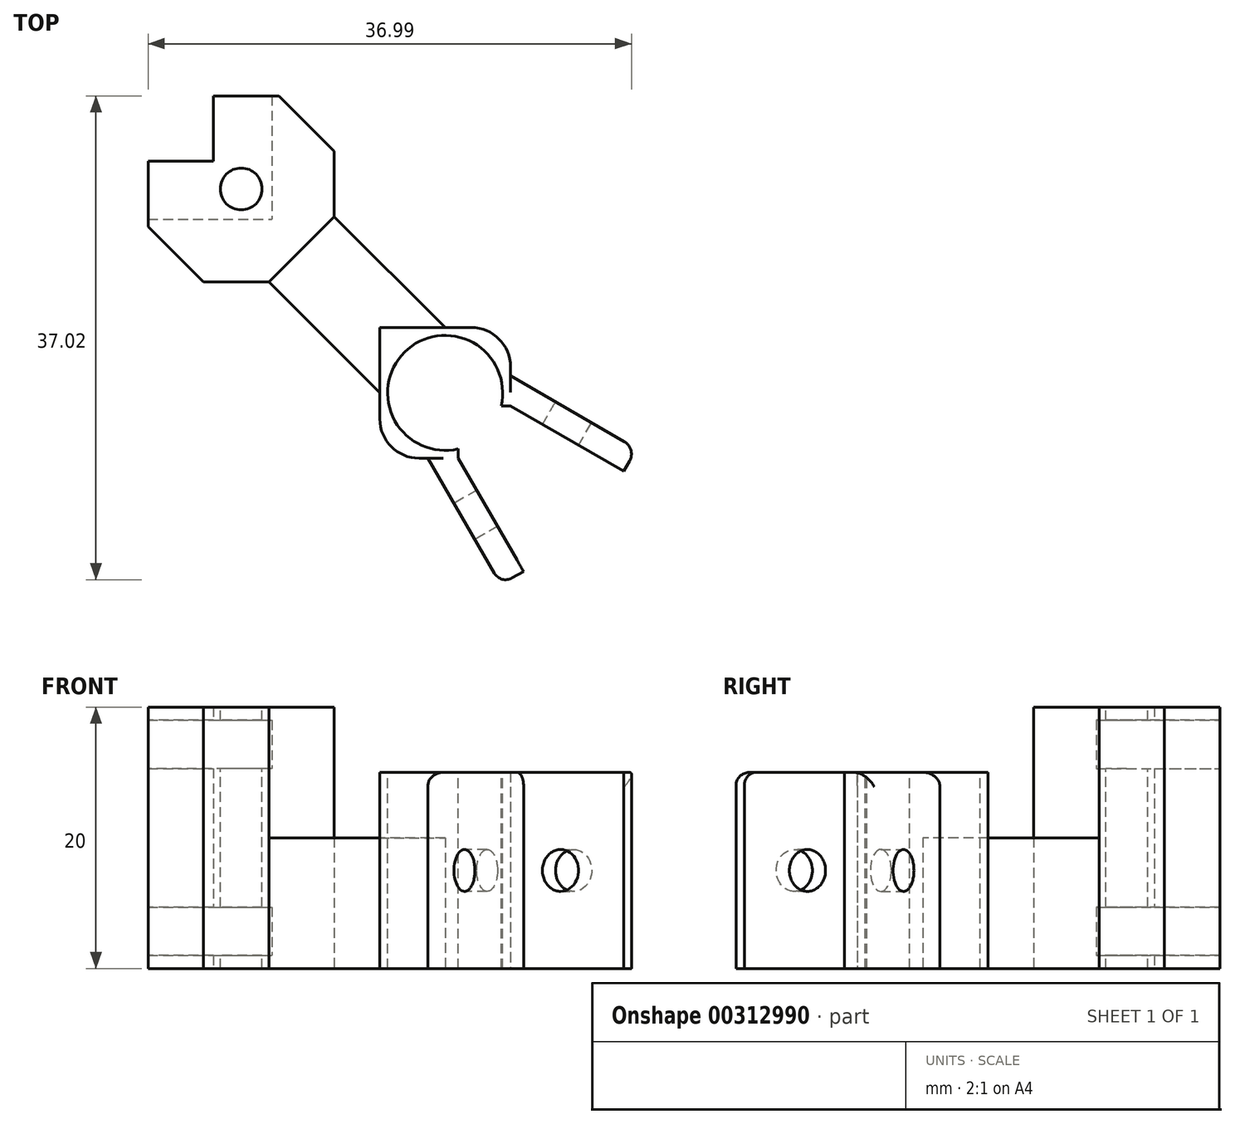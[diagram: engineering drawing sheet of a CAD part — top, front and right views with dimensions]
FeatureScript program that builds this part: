
annotation { "Feature Type Name" : "Feature", "Feature Type Description" : "" }
export const myFeature = defineFeature(function(context is Context, id is Id, definition is map)
    precondition{}
    {
        {
            var Q0;
            Q0=qCreatedBy(makeId("Top.planeOp"),FACE);
            var sketch = newSketch(context, id + "F0", { "sketchPlane" : qUnion([Q0])});
            skLineSegment(sketch, "E0", {"start": v(0, 0) * mm, "end": v(-5, 0) * mm});
            skLineSegment(sketch, "E1", {"start": v(-5, 0) * mm, "end": v(-5, 5) * mm});
            skLineSegment(sketch, "E2", {"start": v(-5, 5) * mm, "end": v(0, 5) * mm});
            skLineSegment(sketch, "E3", {"start": v(0, 5) * mm, "end": v(0, 10) * mm});
            skLineSegment(sketch, "E4", {"start": v(0, 10) * mm, "end": v(5, 10) * mm});
            skLineSegment(sketch, "E5", {"start": v(5, 10) * mm, "end": v(5, 5) * mm});
            skLineSegment(sketch, "E6", {"start": v(-5, 0) * mm, "end": v(-0.76, -4.24) * mm});
            skLineSegment(sketch, "E7", {"start": v(5, 10) * mm, "end": v(9.24, 5.76) * mm});
            skLineSegment(sketch, "E8", {"start": v(9.24, 5.76) * mm, "end": v(9.24, 0.76) * mm});
            skLineSegment(sketch, "E9", {"start": v(-0.76, -4.24) * mm, "end": v(4.24, -4.24) * mm});
            skLineSegment(sketch, "E10", {"start": v(9.24, 0.76) * mm, "end": v(17.73, -7.73) * mm});
            skLineSegment(sketch, "E11", {"start": v(4.24, -4.24) * mm, "end": v(12.73, -12.73) * mm});
            skLineSegment(sketch, "E12", {"start": v(12.73, -12.73) * mm, "end": v(12.73, -17.73) * mm});
            skLineSegment(sketch, "E13", {"start": v(12.73, -17.73) * mm, "end": v(22.73, -17.73) * mm});
            skLineSegment(sketch, "E14", {"start": v(22.73, -17.73) * mm, "end": v(22.73, -7.73) * mm});
            skLineSegment(sketch, "E15", {"start": v(22.73, -7.73) * mm, "end": v(17.73, -7.73) * mm});
            skLineSegment(sketch, "E16", {"start": v(4.24, -4.24) * mm, "end": v(9.24, 0.76) * mm});
            skPoint(sketch, "E17", {"position": v(22.73, -13.73) * mm});
            skPoint(sketch, "E18", {"position": v(18.73, -17.73) * mm});
            skLineSegment(sketch, "E19", {"start": v(22.73, -13.73) * mm, "end": v(31.39, -18.73) * mm});
            skLineSegment(sketch, "E20", {"start": v(18.73, -17.73) * mm, "end": v(23.73, -26.39) * mm});
            skLineSegment(sketch, "E21", {"start": v(31.39, -18.73) * mm, "end": v(32.39, -17) * mm});
            skLineSegment(sketch, "E22", {"start": v(32.39, -17) * mm, "end": v(22.73, -11.42) * mm});
            skLineSegment(sketch, "E23", {"start": v(23.73, -26.39) * mm, "end": v(22, -27.39) * mm});
            skLineSegment(sketch, "E24", {"start": v(22, -27.39) * mm, "end": v(16.42, -17.73) * mm});
            skSolve(sketch);
        }
        {
            var Q0;
            Q0=makeQuery(id+"F0.imprint","IMPRINT",FACE,{"disambiguationData":[TD([[makeQuery(id+"F0.imprint","IMPRINT",EDGE,{"derivedFrom":sQuery(id+"F0.wireOp",EDGE,"E1")}),-1.0]])]});
            extrude(context, id + "F1", {"entities" : qUnion([Q0]), "depth" : 20 * mm});
        }
        {
            var Q0;
            Q0=makeQuery(id+"F0.imprint","IMPRINT",FACE,{"disambiguationData":[TD([[makeQuery(id+"F0.imprint","IMPRINT",EDGE,{"derivedFrom":sQuery(id+"F0.wireOp",EDGE,"E10")}),-1.0]])]});
            extrude(context, id + "F2", {"entities" : qUnion([Q0]), "operationType" : NewBodyOperationType.ADD, "depth" : 10 * mm});
        }
        {
            var Q0;
            Q0=makeQuery(id+"F1.opExtrude","SWEPT_FACE",FACE,{"disambiguationData":[OSD([sQuery(id+"F0.wireOp",EDGE,"E4")])]});
            var sketch = newSketch(context, id + "F3", { "sketchPlane" : qUnion([Q0])});
            skPoint(sketch, "E25", {"position": v(0, 19) * mm});
            skPoint(sketch, "E26", {"position": v(0, 15.6) * mm});
            skPoint(sketch, "E27", {"position": v(0, 1) * mm});
            skPoint(sketch, "E28", {"position": v(0, 4.4) * mm});
            skLineSegment(sketch, "E29", {"start": v(0, 19) * mm, "end": v(-5, 19) * mm});
            skLineSegment(sketch, "E30", {"start": v(-5, 19) * mm, "end": v(-5, 15.6) * mm});
            skLineSegment(sketch, "E31", {"start": v(-5, 15.6) * mm, "end": v(0, 15.6) * mm});
            skSolve(sketch);
        }
        {
            var Q0;
            Q0=qSketchRegion(id+"F3",true);
            var Q1;
            {var subQ0=sQuery(id+"F3.wireOp",EDGE,"E29");Q1=makeQuery(id+"F3.imprint","IMPRINT",FACE,{"disambiguationData":[TD([[makeQuery(id+"F3.imprint","IMPRINT",EDGE,{"derivedFrom":subQ0}),1.0]])]});}
            extrude(context, id + "F4", {"entities" : qUnion([Q0, Q1]), "operationType" : NewBodyOperationType.REMOVE, "oppositeDirection" : true, "depth" : 25 * mm});
        }
        {
            var Q0;
            Q0=makeQuery(id+"F1.opExtrude","SWEPT_FACE",FACE,{"disambiguationData":[OSD([sQuery(id+"F0.wireOp",EDGE,"E2")])]});
            var sketch = newSketch(context, id + "F5", { "sketchPlane" : qUnion([Q0])});
            skLineSegment(sketch, "E32", {"start": v(0, 19) * mm, "end": v(5, 19) * mm});
            skLineSegment(sketch, "E33", {"start": v(5, 19) * mm, "end": v(5, 15.6) * mm});
            skLineSegment(sketch, "E34", {"start": v(5, 15.6) * mm, "end": v(0, 15.6) * mm});
            skLineSegment(sketch, "E35", {"start": v(0, 15.6) * mm, "end": v(0, 19) * mm});
            skSolve(sketch);
        }
        {
            var Q0;
            Q0=makeQuery(id+"F5.imprint","IMPRINT",FACE,{"disambiguationData":[TD([[makeQuery(id+"F5.imprint","IMPRINT",EDGE,{"derivedFrom":sQuery(id+"F5.wireOp",EDGE,"E32")}),-1.0]])]});
            extrude(context, id + "F6", {"entities" : qUnion([Q0]), "operationType" : NewBodyOperationType.REMOVE, "oppositeDirection" : true, "depth" : 25 * mm});
        }
        {
            var Q0;
            Q0=makeQuery(id+"F1.opExtrude","SWEPT_FACE",FACE,{"disambiguationData":[OSD([sQuery(id+"F0.wireOp",EDGE,"E7")])]});
            var sketch = newSketch(context, id + "F7", { "sketchPlane" : qUnion([Q0])});
            skLineSegment(sketch, "E36", {"start": v(3.54, 15.6) * mm, "end": v(-2.46, 15.6) * mm});
            skLineSegment(sketch, "E37", {"start": v(-2.46, 15.6) * mm, "end": v(-2.46, 19) * mm});
            skLineSegment(sketch, "E38", {"start": v(-2.46, 19) * mm, "end": v(3.54, 19) * mm});
            skLineSegment(sketch, "E39", {"start": v(3.54, 19) * mm, "end": v(3.54, 15.6) * mm});
            skSolve(sketch);
        }
        {
            var Q0;
            Q0=qSketchRegion(id+"F7",true);
            extrude(context, id + "F8", {"entities" : qUnion([Q0]), "operationType" : NewBodyOperationType.REMOVE, "oppositeDirection" : true, "depth" : 25 * mm});
        }
        {
            var Q0;
            {var subQ3=sQuery(id+"F0.wireOp",EDGE,"E4");Q0=makeQuery(id+"F4.boolean.opBoolean","SPLIT",FACE,{"disambiguationData":[TD([makeQuery(id+"F4.opExtrude","SWEPT_FACE",FACE,{"disambiguationData":[OSD([sQuery(id+"F3.wireOp",EDGE,"E31")])]})])],"derivedFrom":makeQuery(id+"F1.opExtrude","SWEPT_FACE",FACE,{"disambiguationData":[OSD([subQ3])]})});}
            var sketch = newSketch(context, id + "F9", { "sketchPlane" : qUnion([Q0])});
            skPoint(sketch, "E40", {"position": v(0, 1) * mm});
            skPoint(sketch, "E41", {"position": v(0, 4.4) * mm});
            skLineSegment(sketch, "E42.bottom", {"start": v(0, 4.4) * mm, "end": v(-5, 4.4) * mm});
            skLineSegment(sketch, "E42.top", {"start": v(0, 1) * mm, "end": v(-5, 1) * mm});
            skLineSegment(sketch, "E42.left", {"start": v(0, 4.4) * mm, "end": v(0, 1) * mm});
            skLineSegment(sketch, "E42.right", {"start": v(-5, 4.4) * mm, "end": v(-5, 1) * mm});
            skSolve(sketch);
        }
        {
            var Q0;
            Q0=qSketchRegion(id+"F9",true);
            extrude(context, id + "F10", {"entities" : qUnion([Q0]), "operationType" : NewBodyOperationType.REMOVE, "oppositeDirection" : true, "depth" : 25 * mm});
        }
        {
            var Q0;
            {var subQ3=sQuery(id+"F0.wireOp",EDGE,"E7");Q0=makeQuery(id+"F8.boolean.opBoolean","SPLIT",FACE,{"disambiguationData":[TD([makeQuery(id+"F4.boolean.opBoolean","COPY",FACE,{"derivedFrom":makeQuery(id+"F4.opExtrude","SWEPT_FACE",FACE,{"disambiguationData":[OSD([sQuery(id+"F3.wireOp",EDGE,"E31")])]})})])],"derivedFrom":makeQuery(id+"F1.opExtrude","SWEPT_FACE",FACE,{"disambiguationData":[OSD([subQ3])]})});}
            var sketch = newSketch(context, id + "F11", { "sketchPlane" : qUnion([Q0])});
            skLineSegment(sketch, "E43.bottom", {"start": v(3.54, 1) * mm, "end": v(-2.46, 1) * mm});
            skLineSegment(sketch, "E43.top", {"start": v(3.54, 4.4) * mm, "end": v(-2.46, 4.4) * mm});
            skLineSegment(sketch, "E43.left", {"start": v(3.54, 1) * mm, "end": v(3.54, 4.4) * mm});
            skLineSegment(sketch, "E43.right", {"start": v(-2.46, 1) * mm, "end": v(-2.46, 4.4) * mm});
            skSolve(sketch);
        }
        {
            var Q0;
            Q0=qSketchRegion(id+"F11",true);
            extrude(context, id + "F12", {"entities" : qUnion([Q0]), "operationType" : NewBodyOperationType.REMOVE, "oppositeDirection" : true, "depth" : 25 * mm});
        }
        {
            var Q0;
            {var subQ2=sQuery(id+"F0.wireOp",EDGE,"E2");Q0=makeQuery(id+"F6.boolean.opBoolean","SPLIT",FACE,{"disambiguationData":[TD([makeQuery(id+"F4.boolean.opBoolean","COPY",FACE,{"derivedFrom":makeQuery(id+"F4.opExtrude","SWEPT_FACE",FACE,{"disambiguationData":[OSD([sQuery(id+"F3.wireOp",EDGE,"E31")])]})})])],"derivedFrom":makeQuery(id+"F1.opExtrude","SWEPT_FACE",FACE,{"disambiguationData":[OSD([subQ2])]})});}
            var sketch = newSketch(context, id + "F13", { "sketchPlane" : qUnion([Q0])});
            skLineSegment(sketch, "E44.bottom", {"start": v(0, 4.4) * mm, "end": v(5, 4.4) * mm});
            skLineSegment(sketch, "E44.top", {"start": v(0, 1) * mm, "end": v(5, 1) * mm});
            skLineSegment(sketch, "E44.left", {"start": v(0, 4.4) * mm, "end": v(0, 1) * mm});
            skLineSegment(sketch, "E44.right", {"start": v(5, 4.4) * mm, "end": v(5, 1) * mm});
            skSolve(sketch);
        }
        {
            var Q0;
            Q0=qSketchRegion(id+"F13",true);
            extrude(context, id + "F14", {"entities" : qUnion([Q0]), "operationType" : NewBodyOperationType.REMOVE, "oppositeDirection" : true, "depth" : 25 * mm});
        }
        {
            var Q0;
            Q0=makeQuery(id+"F1.opExtrude","CAP_FACE",FACE,{"disambiguationData":[OSD([sQuery(id+"F0.wireOp",EDGE,"E1"),sQuery(id+"F0.wireOp",EDGE,"E2"),sQuery(id+"F0.wireOp",EDGE,"E3"),sQuery(id+"F0.wireOp",EDGE,"E4"),sQuery(id+"F0.wireOp",EDGE,"E6"),sQuery(id+"F0.wireOp",EDGE,"E7"),sQuery(id+"F0.wireOp",EDGE,"E8"),sQuery(id+"F0.wireOp",EDGE,"E9"),sQuery(id+"F0.wireOp",EDGE,"E16")])],"isStart":false});
            var sketch = newSketch(context, id + "F15", { "sketchPlane" : qUnion([Q0])});
            skLineSegment(sketch, "E45", {"start": v(0, 5) * mm, "end": v(0, 3.17) * mm});
            skLineSegment(sketch, "E46", {"start": v(0, 5) * mm, "end": v(2.05, 5) * mm});
            skLineSegment(sketch, "E47", {"start": v(0, 5) * mm, "end": v(2.12, 2.88) * mm});
            skSolve(sketch);
        }
        {
            var Q0;
            Q0=sQuery(id+"F15.wireOp",VERTEX,"E47.end");
            var Q1;
            Q1=makeQuery(id+"F1.opExtrude","SWEPT_BODY",BODY,{"disambiguationData":[OSD([sQuery(id+"F0.wireOp",EDGE,"E1"),sQuery(id+"F0.wireOp",EDGE,"E2"),sQuery(id+"F0.wireOp",EDGE,"E3"),sQuery(id+"F0.wireOp",EDGE,"E4"),sQuery(id+"F0.wireOp",EDGE,"E6"),sQuery(id+"F0.wireOp",EDGE,"E7"),sQuery(id+"F0.wireOp",EDGE,"E8"),sQuery(id+"F0.wireOp",EDGE,"E9"),sQuery(id+"F0.wireOp",EDGE,"E16")])]});
            hole(context, id + "F16", {"style" : HoleStyle.SIMPLE, "endStyle" : HoleEndStyle.THROUGH, "holeDiameter" : 3.2 * mm, "tappedDepth" : 12 * mm, "tapClearance" : 3, "locations" : qUnion([Q0]), "scope" : qUnion([Q1])});
        }
        {
            var Q0;
            Q0=makeQuery(id+"F2.opExtrude","CAP_FACE",FACE,{"disambiguationData":[OSD([sQuery(id+"F0.wireOp",EDGE,"E10"),sQuery(id+"F0.wireOp",EDGE,"E11"),sQuery(id+"F0.wireOp",EDGE,"E12"),sQuery(id+"F0.wireOp",EDGE,"E13"),sQuery(id+"F0.wireOp",EDGE,"E14"),sQuery(id+"F0.wireOp",EDGE,"E15"),sQuery(id+"F0.wireOp",EDGE,"E16")])],"isStart":false});
            var sketch = newSketch(context, id + "F17", { "sketchPlane" : qUnion([Q0])});
            skLineSegment(sketch, "E48", {"start": v(22.73, -7.73) * mm, "end": v(12.73, -17.73) * mm});
            skLineSegment(sketch, "E49", {"start": v(22.73, -17.73) * mm, "end": v(13.62, -8.62) * mm});
            skPoint(sketch, "E50", {"position": v(17.73, -12.73) * mm});
            skSolve(sketch);
        }
        {
            var Q0;
            Q0=sQuery(id+"F17.wireOp",VERTEX,"E50");
            var Q1;
            Q1=makeQuery(id+"F1.opExtrude","SWEPT_BODY",BODY,{"disambiguationData":[OSD([sQuery(id+"F0.wireOp",EDGE,"E1"),sQuery(id+"F0.wireOp",EDGE,"E2"),sQuery(id+"F0.wireOp",EDGE,"E3"),sQuery(id+"F0.wireOp",EDGE,"E4"),sQuery(id+"F0.wireOp",EDGE,"E6"),sQuery(id+"F0.wireOp",EDGE,"E7"),sQuery(id+"F0.wireOp",EDGE,"E8"),sQuery(id+"F0.wireOp",EDGE,"E9"),sQuery(id+"F0.wireOp",EDGE,"E16")])]});
            hole(context, id + "F18", {"style" : HoleStyle.SIMPLE, "endStyle" : HoleEndStyle.THROUGH, "holeDiameter" : 8.8 * mm, "tappedDepth" : 12 * mm, "tapClearance" : 3, "locations" : qUnion([Q0]), "scope" : qUnion([Q1])});
        }
        {
            var Q0;
            Q0=makeQuery(id+"F2.opExtrude","CAP_FACE",FACE,{"disambiguationData":[OSD([sQuery(id+"F0.wireOp",EDGE,"E10"),sQuery(id+"F0.wireOp",EDGE,"E11"),sQuery(id+"F0.wireOp",EDGE,"E12"),sQuery(id+"F0.wireOp",EDGE,"E13"),sQuery(id+"F0.wireOp",EDGE,"E14"),sQuery(id+"F0.wireOp",EDGE,"E15"),sQuery(id+"F0.wireOp",EDGE,"E16")])],"isStart":false});
            var sketch = newSketch(context, id + "F19", { "sketchPlane" : qUnion([Q0])});
            skLineSegment(sketch, "E51.bottom", {"start": v(22.73, -7.73) * mm, "end": v(12.73, -7.73) * mm});
            skLineSegment(sketch, "E51.top", {"start": v(22.73, -17.73) * mm, "end": v(12.73, -17.73) * mm});
            skLineSegment(sketch, "E51.left", {"start": v(22.73, -7.73) * mm, "end": v(22.73, -17.73) * mm});
            skLineSegment(sketch, "E51.right", {"start": v(12.73, -7.73) * mm, "end": v(12.73, -17.73) * mm});
            skSolve(sketch);
        }
        {
            var Q0;
            {var subQ1=sQuery(id+"F19.wireOp",EDGE,"E51.top");Q0=makeQuery(id+"F19.imprint","IMPRINT",FACE,{"disambiguationData":[TD([[makeQuery(id+"F19.imprint","IMPRINT",EDGE,{"derivedFrom":subQ1}),1.0]])]});}
            extrude(context, id + "F20", {"entities" : qUnion([Q0]), "operationType" : NewBodyOperationType.ADD, "depth" : 5 * mm});
        }
        {
            var Q0;
            Q0=makeQuery(id+"F8.boolean.opBoolean","MERGE",FACE,{"derivedFrom":[makeQuery(id+"F6.boolean.opBoolean","MERGE",FACE,{"derivedFrom":[makeQuery(id+"F4.boolean.opBoolean","COPY",FACE,{"derivedFrom":makeQuery(id+"F4.opExtrude","SWEPT_FACE",FACE,{"disambiguationData":[OSD([sQuery(id+"F3.wireOp",EDGE,"E31")])]})}),makeQuery(id+"F6.opExtrude","SWEPT_FACE",FACE,{"disambiguationData":[OSD([sQuery(id+"F5.wireOp",EDGE,"E34")])]})]}),makeQuery(id+"F8.opExtrude","SWEPT_FACE",FACE,{"disambiguationData":[OSD([sQuery(id+"F7.wireOp",EDGE,"E36")])]})]});
            extrude(context, id + "F21", {"entities" : qUnion([Q0]), "operationType" : NewBodyOperationType.REMOVE, "oppositeDirection" : true, "depth" : 0.3 * mm});
        }
        {
            var Q0;
            Q0=makeQuery(id+"F14.boolean.opBoolean","MERGE",FACE,{"derivedFrom":[makeQuery(id+"F12.boolean.opBoolean","MERGE",FACE,{"derivedFrom":[makeQuery(id+"F10.boolean.opBoolean","COPY",FACE,{"derivedFrom":makeQuery(id+"F10.opExtrude","SWEPT_FACE",FACE,{"disambiguationData":[OSD([sQuery(id+"F9.wireOp",EDGE,"E42.bottom")])]})}),makeQuery(id+"F12.opExtrude","SWEPT_FACE",FACE,{"disambiguationData":[OSD([sQuery(id+"F11.wireOp",EDGE,"E43.top")])]})]}),makeQuery(id+"F14.opExtrude","SWEPT_FACE",FACE,{"disambiguationData":[OSD([sQuery(id+"F13.wireOp",EDGE,"E44.bottom")])]})]});
            extrude(context, id + "F22", {"entities" : qUnion([Q0]), "operationType" : NewBodyOperationType.REMOVE, "oppositeDirection" : true, "depth" : 0.3 * mm});
        }
        {
            var Q0;
            Q0=makeQuery(id+"F20.boolean.opBoolean","MERGE",FACE,{"derivedFrom":[makeQuery(id+"F2.opExtrude","SWEPT_FACE",FACE,{"disambiguationData":[OSD([sQuery(id+"F0.wireOp",EDGE,"E13")])]}),makeQuery(id+"F20.opExtrude","SWEPT_FACE",FACE,{"disambiguationData":[OSD([sQuery(id+"F19.wireOp",EDGE,"E51.top")])]})]});
            var sketch = newSketch(context, id + "F23", { "sketchPlane" : qUnion([Q0])});
            skLineSegment(sketch, "E52", {"start": v(12.79, 15) * mm, "end": v(22.73, 15) * mm});
            skPoint(sketch, "E53", {"position": v(18.73, 15) * mm});
            skLineSegment(sketch, "E54", {"start": v(18.73, 15) * mm, "end": v(18.73, 0) * mm});
            skLineSegment(sketch, "E55", {"start": v(18.73, 0) * mm, "end": v(22.73, 0) * mm});
            skLineSegment(sketch, "E56", {"start": v(22.73, 0) * mm, "end": v(22.73, 15) * mm});
            skSolve(sketch);
        }
        {
            var Q0;
            Q0=makeQuery(id+"F20.boolean.opBoolean","MERGE",FACE,{"derivedFrom":[makeQuery(id+"F2.opExtrude","SWEPT_FACE",FACE,{"disambiguationData":[OSD([sQuery(id+"F0.wireOp",EDGE,"E14")])]}),makeQuery(id+"F20.opExtrude","SWEPT_FACE",FACE,{"disambiguationData":[OSD([sQuery(id+"F19.wireOp",EDGE,"E51.left")])]})]});
            var sketch = newSketch(context, id + "F24", { "sketchPlane" : qUnion([Q0])});
            skLineSegment(sketch, "E57", {"start": v(-17.73, 15) * mm, "end": v(-7.73, 15) * mm});
            skPoint(sketch, "E58", {"position": v(-13.73, 15) * mm});
            skLineSegment(sketch, "E59", {"start": v(-13.73, 15) * mm, "end": v(-13.73, 0) * mm});
            skLineSegment(sketch, "E60", {"start": v(-13.73, 0) * mm, "end": v(-17.73, 0) * mm});
            skLineSegment(sketch, "E61", {"start": v(-17.73, 0) * mm, "end": v(-17.73, 15) * mm});
            skSolve(sketch);
        }
        {
            var Q0;
            Q0=qSketchRegion(id+"F24",true);
            extrude(context, id + "F25", {"entities" : qUnion([Q0]), "operationType" : NewBodyOperationType.REMOVE, "oppositeDirection" : true, "depth" : 2.4 * mm});
        }
        {
            var Q0;
            Q0=qSketchRegion(id+"F23",true);
            extrude(context, id + "F26", {"entities" : qUnion([Q0]), "operationType" : NewBodyOperationType.REMOVE, "oppositeDirection" : true, "depth" : 3.85 * mm});
        }
        {
            var Q0;
            Q0=makeQuery(id+"F20.boolean.opBoolean","MERGE",EDGE,{"derivedFrom":[makeQuery(id+"F2.opExtrude","SWEPT_EDGE",EDGE,{"disambiguationData":[OSD([sQuery(id+"F0.wireOp",EDGE,"E14"),sQuery(id+"F0.wireOp",EDGE,"E15")])]}),makeQuery(id+"F20.opExtrude","SWEPT_EDGE",EDGE,{"disambiguationData":[OSD([sQuery(id+"F19.wireOp",EDGE,"E51.bottom"),sQuery(id+"F19.wireOp",EDGE,"E51.left")])]})]});
            fillet(context, id + "F27", {"entities" : qUnion([Q0]), "radius" : 3 * mm, "tangentPropagation" : true, "allowEdgeOverflow" : false});
        }
        {
            var Q0;
            Q0=makeQuery(id+"F20.boolean.opBoolean","MERGE",EDGE,{"derivedFrom":[makeQuery(id+"F2.opExtrude","SWEPT_EDGE",EDGE,{"disambiguationData":[OSD([sQuery(id+"F0.wireOp",EDGE,"E12"),sQuery(id+"F0.wireOp",EDGE,"E13")])]}),makeQuery(id+"F20.opExtrude","SWEPT_EDGE",EDGE,{"disambiguationData":[OSD([sQuery(id+"F19.wireOp",EDGE,"E51.top"),sQuery(id+"F19.wireOp",EDGE,"E51.right")])]})]});
            fillet(context, id + "F28", {"entities" : qUnion([Q0]), "radius" : 3 * mm, "tangentPropagation" : true, "allowEdgeOverflow" : false});
        }
        {
            var Q0;
            Q0=makeQuery(id+"F21.boolean.opBoolean","COPY",FACE,{"derivedFrom":makeQuery(id+"F21.opExtrude","CAP_FACE",FACE,{"disambiguationData":[OSD([sQuery(id+"F3.wireOp",EDGE,"E31"),sQuery(id+"F5.wireOp",EDGE,"E34"),sQuery(id+"F7.wireOp",EDGE,"E36")])],"isStart":false})});
            var sketch = newSketch(context, id + "F29", { "sketchPlane" : qUnion([Q0])});
            skLineSegment(sketch, "E62", {"start": v(4.45, 0.55) * mm, "end": v(-5, 0.55) * mm});
            skLineSegment(sketch, "E63", {"start": v(4.45, 0.55) * mm, "end": v(4.45, 10) * mm});
            skSolve(sketch);
        }
        {
            var Q0;
            {var subQ6=sQuery(id+"F29.wireOp",EDGE,"E62");Q0=makeQuery(id+"F29.imprint","IMPRINT",FACE,{"disambiguationData":[TD([[makeQuery(id+"F29.imprint","IMPRINT",EDGE,{"derivedFrom":subQ6}),1.0]])]});}
            extrude(context, id + "F30", {"entities" : qUnion([Q0]), "operationType" : NewBodyOperationType.ADD, "depth" : 4 * mm, "hasSecondDirection" : true, "secondDirectionOppositeDirection" : true, "secondDirectionDepth" : 14.72 * mm});
        }
        {
            var Q0;
            {var subQ1=sQuery(id+"F0.wireOp",EDGE,"E9");Q0=makeQuery(id+"F30.boolean.opBoolean","SPLIT",FACE,{"disambiguationData":[TD([makeQuery(id+"F1.opExtrude","SWEPT_FACE",FACE,{"disambiguationData":[OSD([subQ1])]})])],"derivedFrom":makeQuery(id+"F14.boolean.opBoolean","MERGE",FACE,{"derivedFrom":[makeQuery(id+"F12.boolean.opBoolean","MERGE",FACE,{"derivedFrom":[makeQuery(id+"F10.boolean.opBoolean","COPY",FACE,{"derivedFrom":makeQuery(id+"F10.opExtrude","SWEPT_FACE",FACE,{"disambiguationData":[OSD([sQuery(id+"F9.wireOp",EDGE,"E42.top")])]})}),makeQuery(id+"F12.opExtrude","SWEPT_FACE",FACE,{"disambiguationData":[OSD([sQuery(id+"F11.wireOp",EDGE,"E43.bottom")])]})]}),makeQuery(id+"F14.opExtrude","SWEPT_FACE",FACE,{"disambiguationData":[OSD([sQuery(id+"F13.wireOp",EDGE,"E44.top")])]})]})});}
            extrude(context, id + "F31", {"entities" : qUnion([Q0]), "operationType" : NewBodyOperationType.ADD, "depth" : 4.73 * mm});
        }
        {
            var Q0;
            {var subQ0=sQuery(id+"F0.wireOp",EDGE,"E20");Q0=makeQuery(id+"F0.imprint","IMPRINT",FACE,{"disambiguationData":[TD([[makeQuery(id+"F0.imprint","IMPRINT",EDGE,{"derivedFrom":subQ0}),-1.0]])]});}
            var Q1;
            {var subQ0=sQuery(id+"F0.wireOp",EDGE,"E19");Q1=makeQuery(id+"F0.imprint","IMPRINT",FACE,{"disambiguationData":[TD([[makeQuery(id+"F0.imprint","IMPRINT",EDGE,{"derivedFrom":subQ0}),1.0]])]});}
            extrude(context, id + "F32", {"entities" : qUnion([Q0, Q1]), "operationType" : NewBodyOperationType.ADD, "depth" : 15 * mm});
        }
        {
            var Q0;
            Q0=makeQuery(id+"F32.opExtrude","SWEPT_FACE",FACE,{"disambiguationData":[OSD([sQuery(id+"F0.wireOp",EDGE,"E22")])]});
            var sketch = newSketch(context, id + "F33", { "sketchPlane" : qUnion([Q0])});
            skLineSegment(sketch, "E64", {"start": v(-25.4, 15) * mm, "end": v(-36.55, 0) * mm});
            skLineSegment(sketch, "E65", {"start": v(-36.55, 15) * mm, "end": v(-25.4, 0) * mm});
            skPoint(sketch, "E66", {"position": v(-30.97, 7.5) * mm});
            skSolve(sketch);
        }
        {
            var Q0;
            Q0=sQuery(id+"F33.wireOp",VERTEX,"E66");
            var Q1;
            Q1=makeQuery(id+"F1.opExtrude","SWEPT_BODY",BODY,{"disambiguationData":[OSD([sQuery(id+"F0.wireOp",EDGE,"E1"),sQuery(id+"F0.wireOp",EDGE,"E2"),sQuery(id+"F0.wireOp",EDGE,"E3"),sQuery(id+"F0.wireOp",EDGE,"E4"),sQuery(id+"F0.wireOp",EDGE,"E6"),sQuery(id+"F0.wireOp",EDGE,"E7"),sQuery(id+"F0.wireOp",EDGE,"E8"),sQuery(id+"F0.wireOp",EDGE,"E9"),sQuery(id+"F0.wireOp",EDGE,"E16")])]});
            hole(context, id + "F34", {"style" : HoleStyle.SIMPLE, "endStyle" : HoleEndStyle.BLIND, "holeDiameter" : 3.2 * mm, "holeDepth" : 5 * mm, "tappedDepth" : 12 * mm, "tapClearance" : 3, "locations" : qUnion([Q0]), "scope" : qUnion([Q1])});
        }
        {
            var Q0;
            Q0=makeQuery(id+"F32.opExtrude","SWEPT_FACE",FACE,{"disambiguationData":[OSD([sQuery(id+"F0.wireOp",EDGE,"E24")])]});
            var sketch = newSketch(context, id + "F35", { "sketchPlane" : qUnion([Q0])});
            skLineSegment(sketch, "E67", {"start": v(23.56, 15) * mm, "end": v(34.72, 0) * mm});
            skLineSegment(sketch, "E68", {"start": v(34.72, 15) * mm, "end": v(23.56, 0) * mm});
            skPoint(sketch, "E69", {"position": v(29.14, 7.5) * mm});
            skSolve(sketch);
        }
        {
            var Q0;
            Q0=sQuery(id+"F35.wireOp",VERTEX,"E69");
            var Q1;
            Q1=makeQuery(id+"F1.opExtrude","SWEPT_BODY",BODY,{"disambiguationData":[OSD([sQuery(id+"F0.wireOp",EDGE,"E1"),sQuery(id+"F0.wireOp",EDGE,"E2"),sQuery(id+"F0.wireOp",EDGE,"E3"),sQuery(id+"F0.wireOp",EDGE,"E4"),sQuery(id+"F0.wireOp",EDGE,"E6"),sQuery(id+"F0.wireOp",EDGE,"E7"),sQuery(id+"F0.wireOp",EDGE,"E8"),sQuery(id+"F0.wireOp",EDGE,"E9"),sQuery(id+"F0.wireOp",EDGE,"E16")])]});
            hole(context, id + "F36", {"style" : HoleStyle.SIMPLE, "endStyle" : HoleEndStyle.BLIND, "holeDiameter" : 3.2 * mm, "holeDepth" : 5 * mm, "tappedDepth" : 12 * mm, "tapClearance" : 3, "locations" : qUnion([Q0]), "scope" : qUnion([Q1])});
        }
        {
            var Q0;
            Q0=makeQuery(id+"F32.opExtrude","CAP_EDGE",EDGE,{"disambiguationData":[OSD([sQuery(id+"F0.wireOp",EDGE,"E24")])],"isStart":false});
            fillet(context, id + "F37", {"entities" : qUnion([Q0]), "radius" : 1 * mm, "tangentPropagation" : true, "allowEdgeOverflow" : false});
        }
        {
            var Q0;
            Q0=makeQuery(id+"F32.opExtrude","SWEPT_EDGE",EDGE,{"disambiguationData":[OSD([sQuery(id+"F0.wireOp",EDGE,"E23"),sQuery(id+"F0.wireOp",EDGE,"E24")])]});
            fillet(context, id + "F38", {"entities" : qUnion([Q0]), "radius" : 1 * mm, "tangentPropagation" : true, "allowEdgeOverflow" : false});
        }
        {
            var Q0;
            Q0=makeQuery(id+"F32.opExtrude","CAP_EDGE",EDGE,{"disambiguationData":[OSD([sQuery(id+"F0.wireOp",EDGE,"E22")])],"isStart":false});
            var Q1;
            Q1=makeQuery(id+"F32.opExtrude","SWEPT_EDGE",EDGE,{"disambiguationData":[OSD([sQuery(id+"F0.wireOp",EDGE,"E21"),sQuery(id+"F0.wireOp",EDGE,"E22")])]});
            fillet(context, id + "F39", {"entities" : qUnion([Q0, Q1]), "radius" : 1.1 * mm, "tangentPropagation" : true, "allowEdgeOverflow" : false});
        }
    });
